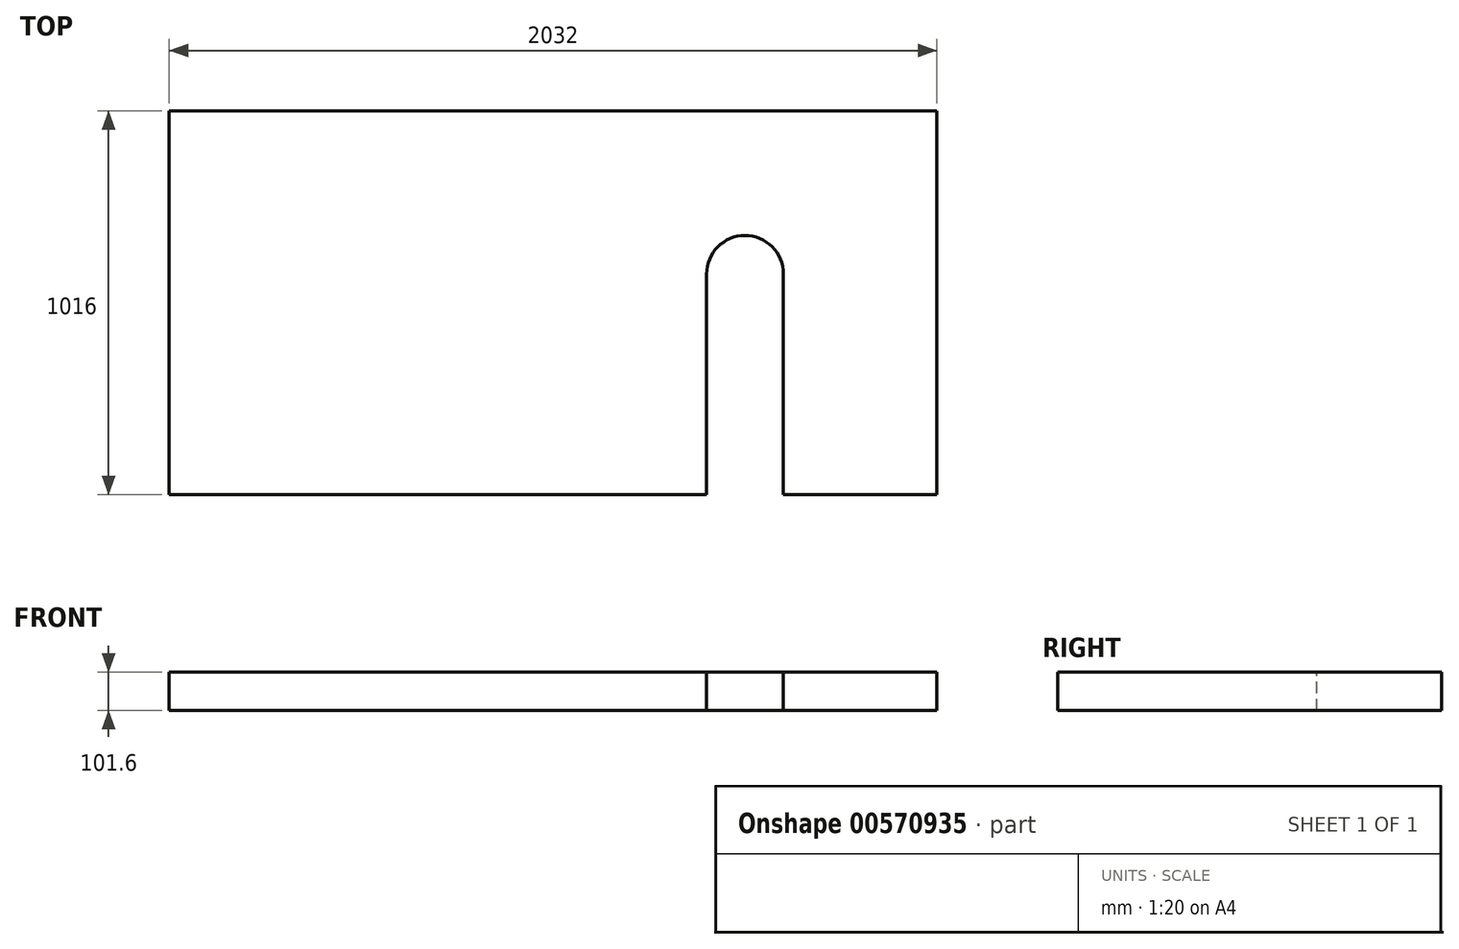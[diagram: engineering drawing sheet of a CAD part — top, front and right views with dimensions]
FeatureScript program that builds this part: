
annotation { "Feature Type Name" : "Feature", "Feature Type Description" : "" }
export const myFeature = defineFeature(function(context is Context, id is Id, definition is map)
    precondition{}
    {
        {
            var Q0;
            Q0=qCreatedBy(makeId("Top.planeOp"),FACE);
            var sketch = newSketch(context, id + "F0", { "sketchPlane" : qUnion([Q0])});
            skLineSegment(sketch, "E0.bottom", {"start": v(0, 0) * mm, "end": v(2032, 0) * mm});
            skLineSegment(sketch, "E0.top", {"start": v(0, 1016) * mm, "end": v(2032, 1016) * mm});
            skLineSegment(sketch, "E0.left", {"start": v(0, 0) * mm, "end": v(0, 1016) * mm});
            skLineSegment(sketch, "E0.right", {"start": v(2032, 0) * mm, "end": v(2032, 1016) * mm});
            skSolve(sketch);
        }
        {
            var Q0;
            Q0 = qSketchRegion(id + "F0", true);
            extrude(context, id + "F1", {"entities" : qUnion([Q0]), "depth" : 101.6 * mm, "offsetDistance" : 25.4 * mm});
        }
        {
            var Q0;
            Q0=makeQuery(id+"F1.opExtrude","CAP_FACE",FACE,{"disambiguationData":[OSD([sQuery(id+"F0.wireOp",EDGE,"E0.bottom"),sQuery(id+"F0.wireOp",EDGE,"E0.top"),sQuery(id+"F0.wireOp",EDGE,"E0.left"),sQuery(id+"F0.wireOp",EDGE,"E0.right")])],"isStart":false});
            var sketch = newSketch(context, id + "F2", { "sketchPlane" : qUnion([Q0])});
            skLineSegment(sketch, "E1", {"start": v(1422.4, 0) * mm, "end": v(1422.4, 584.2) * mm});
            skLineSegment(sketch, "E2", {"start": v(1625.6, 0) * mm, "end": v(1625.6, 584.2) * mm});
            skArc(sketch, "E3", {"start": v(1625.6, 584.2) * mm, "mid": v(1524, 685.8) * mm, "end": v(1422.4, 584.2) * mm});
            skLineSegment(sketch, "E4", {"start": v(1422.4, 0) * mm, "end": v(1625.6, 0) * mm});
            skLineSegment(sketch, "E5", {"start": v(1524, 806.3) * mm, "end": v(1524, 279.18) * mm, "construction": true});
            skSolve(sketch);
        }
        {
            var Q0;
            Q0 = qSketchRegion(id + "F2", true);
            extrude(context, id + "F3", {"entities" : qUnion([Q0]), "operationType" : NewBodyOperationType.REMOVE, "endBound" : BoundingType.THROUGH_ALL, "oppositeDirection" : true, "depth" : 25.4 * mm, "offsetDistance" : 25.4 * mm});
        }
    });
